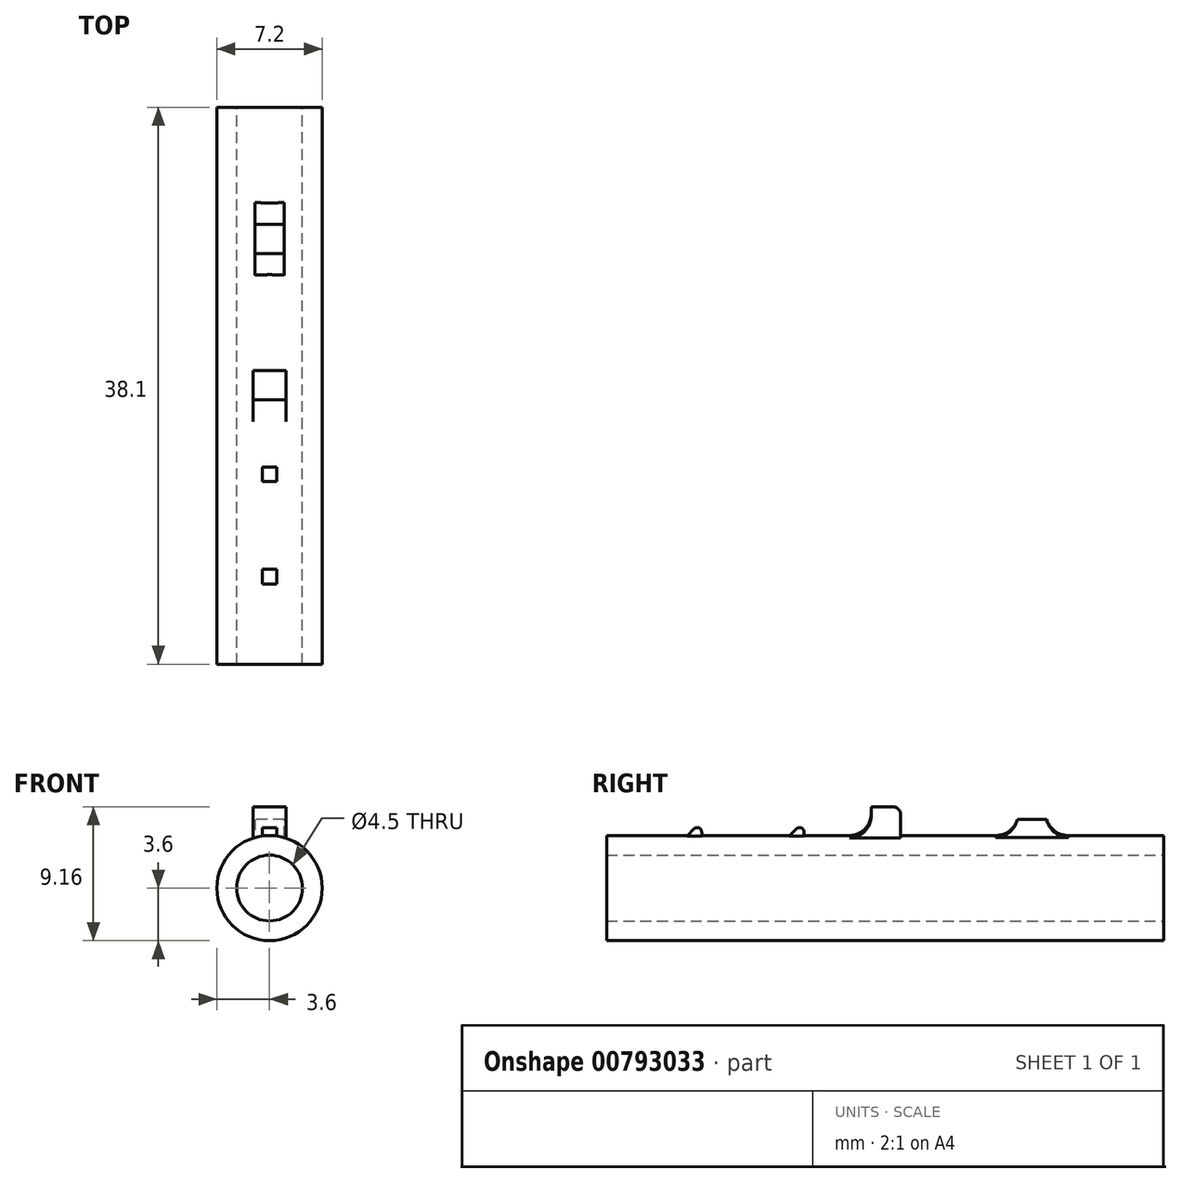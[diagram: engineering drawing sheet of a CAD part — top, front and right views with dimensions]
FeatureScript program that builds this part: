
annotation { "Feature Type Name" : "Feature", "Feature Type Description" : "" }
export const myFeature = defineFeature(function(context is Context, id is Id, definition is map)
    precondition{}
    {
        {
            var Q0;
            Q0=qCreatedBy(makeId("Front.planeOp"),FACE);
            var sketch = newSketch(context, id + "F0", { "sketchPlane" : qUnion([Q0])});
            skCircle(sketch, "E0", {"center": v(0, 0) * mm, "radius": 2.25 * mm});
            skCircle(sketch, "E1", {"center": v(0, 0) * mm, "radius": 3.6 * mm});
            skSolve(sketch);
        }
        {
            var Q0;
            Q0=makeQuery(id+"F0.imprint","IMPRINT",FACE,{"disambiguationData":[TD([[makeQuery(id+"F0.imprint","IMPRINT",EDGE,{"derivedFrom":sQuery(id+"F0.wireOp",EDGE,"E0")}),-1.0]])]});
            extrude(context, id + "F1", {"entities" : qUnion([Q0]), "depth" : 37.6 * mm, "offsetDistance" : 25.4 * mm});
        }
        {
            var Q0;
            Q0=makeQuery(id+"F1.opExtrude","CAP_FACE",FACE,{"disambiguationData":[OSD([sQuery(id+"F0.wireOp",EDGE,"E0"),sQuery(id+"F0.wireOp",EDGE,"E1")])],"isStart":false});
            var sketch = newSketch(context, id + "F2", { "sketchPlane" : qUnion([Q0])});
            skLineSegment(sketch, "E2.bottom", {"start": v(1, 4.71) * mm, "end": v(-1, 4.71) * mm});
            skLineSegment(sketch, "E2.left", {"start": v(1, 4.71) * mm, "end": v(1, 3.46) * mm});
            skLineSegment(sketch, "E2.right", {"start": v(-1, 4.71) * mm, "end": v(-1, 3.46) * mm});
            skPoint(sketch, "E2.middle", {"position": v(0, 3.6) * mm});
            skPoint(sketch, "E3", {"position": v(-1, 3.46) * mm});
            skPoint(sketch, "E4", {"position": v(1, 3.46) * mm});
            skPoint(sketch, "E2.top.end.orphan", {"position": v(-1, 2.49) * mm});
            skPoint(sketch, "E5.orphan", {"position": v(1, 2.49) * mm});
            skSolve(sketch);
        }
        {
            var Q0;
            Q0=makeQuery(id+"F2.imprint","IMPRINT",FACE,{"disambiguationData":[TD([[makeQuery(id+"F2.imprint","IMPRINT",EDGE,{"derivedFrom":sQuery(id+"F2.wireOp",EDGE,"E2.bottom")}),1.0]])]});
            extrude(context, id + "F3", {"entities" : qUnion([Q0]), "operationType" : NewBodyOperationType.ADD, "oppositeDirection" : true, "depth" : 37.05 * mm, "offsetDistance" : 25 * mm});
        }
        {
            var Q0;
            {var subQ0=sQuery(id+"F0.wireOp",EDGE,"E1");Q0=makeQuery(id+"F3.boolean.opBoolean","MERGE",FACE,{"derivedFrom":[makeQuery(id+"F1.opExtrude","CAP_FACE",FACE,{"disambiguationData":[OSD([sQuery(id+"F0.wireOp",EDGE,"E0"),subQ0])],"isStart":false}),makeQuery(id+"F3.opExtrude","CAP_FACE",FACE,{"disambiguationData":[OSD([subQ0,sQuery(id+"F2.wireOp",EDGE,"E2.bottom"),sQuery(id+"F2.wireOp",EDGE,"E2.left"),sQuery(id+"F2.wireOp",EDGE,"E2.right")])],"isStart":true})]});}
            var sketch = newSketch(context, id + "F4", { "sketchPlane" : qUnion([Q0])});
            skCircle(sketch, "E6", {"center": v(0, 0) * mm, "radius": 3.6 * mm});
            skSolve(sketch);
        }
        {
            var Q0;
            Q0=makeQuery(id+"F4.imprint","IMPRINT",FACE,{"disambiguationData":[TD([[makeQuery(id+"F4.imprint","IMPRINT",EDGE,{"derivedFrom":makeQuery(id+"F3.opExtrude","CAP_EDGE",EDGE,{"disambiguationData":[OSD([sQuery(id+"F2.wireOp",EDGE,"E2.bottom")])],"isStart":true})}),1.0]])]});
            extrude(context, id + "F5", {"entities" : qUnion([Q0]), "operationType" : NewBodyOperationType.REMOVE, "oppositeDirection" : true, "depth" : 27.6 * mm, "offsetDistance" : 25 * mm});
        }
        {
            var Q0;
            Q0=makeQuery(id+"F3.opExtrude","CAP_FACE",FACE,{"disambiguationData":[OSD([sQuery(id+"F0.wireOp",EDGE,"E1"),sQuery(id+"F2.wireOp",EDGE,"E2.bottom"),sQuery(id+"F2.wireOp",EDGE,"E2.left"),sQuery(id+"F2.wireOp",EDGE,"E2.right")])],"isStart":false});
            extrude(context, id + "F6", {"entities" : qUnion([Q0]), "operationType" : NewBodyOperationType.REMOVE, "oppositeDirection" : true, "depth" : 7.45 * mm, "offsetDistance" : 25 * mm});
        }
        {
            var Q0;
            {var subQ0=sQuery(id+"F0.wireOp",EDGE,"E1");Q0=makeQuery(id+"F3.boolean.opBoolean","MERGE",FACE,{"derivedFrom":[makeQuery(id+"F1.opExtrude","CAP_FACE",FACE,{"disambiguationData":[OSD([sQuery(id+"F0.wireOp",EDGE,"E0"),subQ0])],"isStart":false}),makeQuery(id+"F3.opExtrude","CAP_FACE",FACE,{"disambiguationData":[OSD([subQ0,sQuery(id+"F2.wireOp",EDGE,"E2.bottom"),sQuery(id+"F2.wireOp",EDGE,"E2.left"),sQuery(id+"F2.wireOp",EDGE,"E2.right")])],"isStart":true})]});}
            var sketch = newSketch(context, id + "F7", { "sketchPlane" : qUnion([Q0])});
            skLineSegment(sketch, "E7.bottom", {"start": v(1.12, 5.56) * mm, "end": v(-1.12, 5.56) * mm});
            skLineSegment(sketch, "E7.left", {"start": v(1.12, 5.56) * mm, "end": v(1.12, 3.42) * mm});
            skLineSegment(sketch, "E7.right", {"start": v(-1.12, 5.56) * mm, "end": v(-1.12, 3.42) * mm});
            skPoint(sketch, "E7.middle", {"position": v(0, 3.6) * mm});
            skPoint(sketch, "E8", {"position": v(-1.12, 3.42) * mm});
            skPoint(sketch, "E9", {"position": v(1.12, 3.42) * mm});
            skPoint(sketch, "E7.top.end.orphan", {"position": v(-1.12, 1.64) * mm});
            skPoint(sketch, "E10.orphan", {"position": v(1.12, 1.64) * mm});
            skCircle(sketch, "E11", {"center": v(0, 0) * mm, "radius": 3.6 * mm});
            skSolve(sketch);
        }
        {
            var Q0;
            Q0=makeQuery(id+"F7.imprint","IMPRINT",FACE,{"disambiguationData":[TD([[makeQuery(id+"F7.imprint","IMPRINT",EDGE,{"derivedFrom":sQuery(id+"F7.wireOp",EDGE,"E7.bottom")}),1.0]])]});
            extrude(context, id + "F8", {"entities" : qUnion([Q0]), "operationType" : NewBodyOperationType.ADD, "oppositeDirection" : true, "depth" : 19.6 * mm, "offsetDistance" : 25 * mm});
        }
        {
            var Q0;
            {var subQ0=sQuery(id+"F0.wireOp",EDGE,"E1");Q0=makeQuery(id+"F8.boolean.opBoolean","MERGE",FACE,{"derivedFrom":[makeQuery(id+"F3.boolean.opBoolean","MERGE",FACE,{"derivedFrom":[makeQuery(id+"F1.opExtrude","CAP_FACE",FACE,{"disambiguationData":[OSD([sQuery(id+"F0.wireOp",EDGE,"E0"),subQ0])],"isStart":false}),makeQuery(id+"F3.opExtrude","CAP_FACE",FACE,{"disambiguationData":[OSD([subQ0,sQuery(id+"F2.wireOp",EDGE,"E2.bottom"),sQuery(id+"F2.wireOp",EDGE,"E2.left"),sQuery(id+"F2.wireOp",EDGE,"E2.right")])],"isStart":true})]}),makeQuery(id+"F8.opExtrude","CAP_FACE",FACE,{"disambiguationData":[OSD([sQuery(id+"F7.wireOp",EDGE,"E7.bottom"),sQuery(id+"F7.wireOp",EDGE,"E7.left"),sQuery(id+"F7.wireOp",EDGE,"E7.right"),sQuery(id+"F7.wireOp",EDGE,"E11")])],"isStart":true})]});}
            var sketch = newSketch(context, id + "F9", { "sketchPlane" : qUnion([Q0])});
            skCircle(sketch, "E12", {"center": v(0, 0) * mm, "radius": 3.6 * mm});
            skSolve(sketch);
        }
        {
            var Q0;
            Q0=makeQuery(id+"F9.imprint","IMPRINT",FACE,{"disambiguationData":[TD([[makeQuery(id+"F9.imprint","IMPRINT",EDGE,{"derivedFrom":makeQuery(id+"F8.opExtrude","CAP_EDGE",EDGE,{"disambiguationData":[OSD([sQuery(id+"F7.wireOp",EDGE,"E7.bottom")])],"isStart":true})}),1.0]])]});
            extrude(context, id + "F10", {"entities" : qUnion([Q0]), "operationType" : NewBodyOperationType.REMOVE, "oppositeDirection" : true, "depth" : 17.6 * mm, "offsetDistance" : 25 * mm});
        }
        {
            var Q0;
            {var subQ0=sQuery(id+"F0.wireOp",EDGE,"E1");Q0=makeQuery(id+"F8.boolean.opBoolean","MERGE",FACE,{"derivedFrom":[makeQuery(id+"F3.boolean.opBoolean","MERGE",FACE,{"derivedFrom":[makeQuery(id+"F1.opExtrude","CAP_FACE",FACE,{"disambiguationData":[OSD([sQuery(id+"F0.wireOp",EDGE,"E0"),subQ0])],"isStart":false}),makeQuery(id+"F3.opExtrude","CAP_FACE",FACE,{"disambiguationData":[OSD([subQ0,sQuery(id+"F2.wireOp",EDGE,"E2.bottom"),sQuery(id+"F2.wireOp",EDGE,"E2.left"),sQuery(id+"F2.wireOp",EDGE,"E2.right")])],"isStart":true})]}),makeQuery(id+"F8.opExtrude","CAP_FACE",FACE,{"disambiguationData":[OSD([sQuery(id+"F7.wireOp",EDGE,"E7.bottom"),sQuery(id+"F7.wireOp",EDGE,"E7.left"),sQuery(id+"F7.wireOp",EDGE,"E7.right"),sQuery(id+"F7.wireOp",EDGE,"E11")])],"isStart":true})]});}
            var sketch = newSketch(context, id + "F11", { "sketchPlane" : qUnion([Q0])});
            skLineSegment(sketch, "E13.bottom", {"start": v(0.5, 4.57) * mm, "end": v(-0.5, 4.57) * mm});
            skLineSegment(sketch, "E13.left", {"start": v(0.5, 4.57) * mm, "end": v(0.5, 3.57) * mm});
            skLineSegment(sketch, "E13.right", {"start": v(-0.5, 4.57) * mm, "end": v(-0.5, 3.57) * mm});
            skPoint(sketch, "E13.middle", {"position": v(0, 3.6) * mm});
            skPoint(sketch, "E14", {"position": v(-0.5, 3.57) * mm});
            skPoint(sketch, "E15", {"position": v(0.5, 3.57) * mm});
            skPoint(sketch, "E13.top.end.orphan", {"position": v(-0.5, 2.63) * mm});
            skPoint(sketch, "E16.orphan", {"position": v(0.5, 2.63) * mm});
            skCircle(sketch, "E17", {"center": v(0, 0) * mm, "radius": 3.6 * mm});
            skSolve(sketch);
        }
        {
            var Q0;
            Q0=makeQuery(id+"F11.imprint","IMPRINT",FACE,{"disambiguationData":[TD([[makeQuery(id+"F11.imprint","IMPRINT",EDGE,{"derivedFrom":sQuery(id+"F11.wireOp",EDGE,"E13.bottom")}),1.0]])]});
            extrude(context, id + "F12", {"entities" : qUnion([Q0]), "operationType" : NewBodyOperationType.ADD, "oppositeDirection" : true, "depth" : 13 * mm, "offsetDistance" : 25 * mm});
        }
        {
            var Q0;
            {var subQ0=sQuery(id+"F0.wireOp",EDGE,"E1");Q0=makeQuery(id+"F12.boolean.opBoolean","MERGE",FACE,{"derivedFrom":[makeQuery(id+"F8.boolean.opBoolean","MERGE",FACE,{"derivedFrom":[makeQuery(id+"F3.boolean.opBoolean","MERGE",FACE,{"derivedFrom":[makeQuery(id+"F1.opExtrude","CAP_FACE",FACE,{"disambiguationData":[OSD([sQuery(id+"F0.wireOp",EDGE,"E0"),subQ0])],"isStart":false}),makeQuery(id+"F3.opExtrude","CAP_FACE",FACE,{"disambiguationData":[OSD([subQ0,sQuery(id+"F2.wireOp",EDGE,"E2.bottom"),sQuery(id+"F2.wireOp",EDGE,"E2.left"),sQuery(id+"F2.wireOp",EDGE,"E2.right")])],"isStart":true})]}),makeQuery(id+"F8.opExtrude","CAP_FACE",FACE,{"disambiguationData":[OSD([sQuery(id+"F7.wireOp",EDGE,"E7.bottom"),sQuery(id+"F7.wireOp",EDGE,"E7.left"),sQuery(id+"F7.wireOp",EDGE,"E7.right"),sQuery(id+"F7.wireOp",EDGE,"E11")])],"isStart":true})]}),makeQuery(id+"F12.opExtrude","CAP_FACE",FACE,{"disambiguationData":[OSD([sQuery(id+"F11.wireOp",EDGE,"E13.bottom"),sQuery(id+"F11.wireOp",EDGE,"E13.left"),sQuery(id+"F11.wireOp",EDGE,"E13.right"),sQuery(id+"F11.wireOp",EDGE,"E17")])],"isStart":true})]});}
            var sketch = newSketch(context, id + "F13", { "sketchPlane" : qUnion([Q0])});
            skCircle(sketch, "E18", {"center": v(0, 0) * mm, "radius": 3.6 * mm});
            skSolve(sketch);
        }
        {
            var Q0;
            Q0=makeQuery(id+"F13.imprint","IMPRINT",FACE,{"disambiguationData":[TD([[makeQuery(id+"F13.imprint","IMPRINT",EDGE,{"derivedFrom":makeQuery(id+"F12.opExtrude","CAP_EDGE",EDGE,{"disambiguationData":[OSD([sQuery(id+"F11.wireOp",EDGE,"E13.bottom")])],"isStart":true})}),1.0]])]});
            extrude(context, id + "F14", {"entities" : qUnion([Q0]), "operationType" : NewBodyOperationType.REMOVE, "oppositeDirection" : true, "depth" : 12 * mm, "offsetDistance" : 25 * mm});
        }
        {
            var Q0;
            {var subQ0=sQuery(id+"F0.wireOp",EDGE,"E1");Q0=makeQuery(id+"F12.boolean.opBoolean","MERGE",FACE,{"derivedFrom":[makeQuery(id+"F8.boolean.opBoolean","MERGE",FACE,{"derivedFrom":[makeQuery(id+"F3.boolean.opBoolean","MERGE",FACE,{"derivedFrom":[makeQuery(id+"F1.opExtrude","CAP_FACE",FACE,{"disambiguationData":[OSD([sQuery(id+"F0.wireOp",EDGE,"E0"),subQ0])],"isStart":false}),makeQuery(id+"F3.opExtrude","CAP_FACE",FACE,{"disambiguationData":[OSD([subQ0,sQuery(id+"F2.wireOp",EDGE,"E2.bottom"),sQuery(id+"F2.wireOp",EDGE,"E2.left"),sQuery(id+"F2.wireOp",EDGE,"E2.right")])],"isStart":true})]}),makeQuery(id+"F8.opExtrude","CAP_FACE",FACE,{"disambiguationData":[OSD([sQuery(id+"F7.wireOp",EDGE,"E7.bottom"),sQuery(id+"F7.wireOp",EDGE,"E7.left"),sQuery(id+"F7.wireOp",EDGE,"E7.right"),sQuery(id+"F7.wireOp",EDGE,"E11")])],"isStart":true})]}),makeQuery(id+"F12.opExtrude","CAP_FACE",FACE,{"disambiguationData":[OSD([sQuery(id+"F11.wireOp",EDGE,"E13.bottom"),sQuery(id+"F11.wireOp",EDGE,"E13.left"),sQuery(id+"F11.wireOp",EDGE,"E13.right"),sQuery(id+"F11.wireOp",EDGE,"E17")])],"isStart":true})]});}
            var sketch = newSketch(context, id + "F15", { "sketchPlane" : qUnion([Q0])});
            skLineSegment(sketch, "E19.bottom", {"start": v(0.5, 4.57) * mm, "end": v(-0.5, 4.57) * mm});
            skLineSegment(sketch, "E19.left", {"start": v(0.5, 4.57) * mm, "end": v(0.5, 3.57) * mm});
            skLineSegment(sketch, "E19.right", {"start": v(-0.5, 4.57) * mm, "end": v(-0.5, 3.57) * mm});
            skPoint(sketch, "E19.middle", {"position": v(0, 3.6) * mm});
            skPoint(sketch, "E20", {"position": v(-0.5, 3.57) * mm});
            skPoint(sketch, "E21", {"position": v(0.5, 3.57) * mm});
            skPoint(sketch, "E19.top.end.orphan", {"position": v(-0.5, 2.63) * mm});
            skPoint(sketch, "E22.orphan", {"position": v(0.5, 2.63) * mm});
            skSolve(sketch);
        }
        {
            var Q0;
            Q0=makeQuery(id+"F15.imprint","IMPRINT",FACE,{"disambiguationData":[TD([[makeQuery(id+"F15.imprint","IMPRINT",EDGE,{"derivedFrom":sQuery(id+"F15.wireOp",EDGE,"E19.bottom")}),1.0]])]});
            extrude(context, id + "F16", {"entities" : qUnion([Q0]), "operationType" : NewBodyOperationType.ADD, "oppositeDirection" : true, "depth" : 6 * mm, "offsetDistance" : 25 * mm});
        }
        {
            var Q0;
            {var subQ0=sQuery(id+"F0.wireOp",EDGE,"E1");Q0=makeQuery(id+"F16.boolean.opBoolean","MERGE",FACE,{"derivedFrom":[makeQuery(id+"F12.boolean.opBoolean","MERGE",FACE,{"derivedFrom":[makeQuery(id+"F8.boolean.opBoolean","MERGE",FACE,{"derivedFrom":[makeQuery(id+"F3.boolean.opBoolean","MERGE",FACE,{"derivedFrom":[makeQuery(id+"F1.opExtrude","CAP_FACE",FACE,{"disambiguationData":[OSD([sQuery(id+"F0.wireOp",EDGE,"E0"),subQ0])],"isStart":false}),makeQuery(id+"F3.opExtrude","CAP_FACE",FACE,{"disambiguationData":[OSD([subQ0,sQuery(id+"F2.wireOp",EDGE,"E2.bottom"),sQuery(id+"F2.wireOp",EDGE,"E2.left"),sQuery(id+"F2.wireOp",EDGE,"E2.right")])],"isStart":true})]}),makeQuery(id+"F8.opExtrude","CAP_FACE",FACE,{"disambiguationData":[OSD([sQuery(id+"F7.wireOp",EDGE,"E7.bottom"),sQuery(id+"F7.wireOp",EDGE,"E7.left"),sQuery(id+"F7.wireOp",EDGE,"E7.right"),sQuery(id+"F7.wireOp",EDGE,"E11")])],"isStart":true})]}),makeQuery(id+"F12.opExtrude","CAP_FACE",FACE,{"disambiguationData":[OSD([sQuery(id+"F11.wireOp",EDGE,"E13.bottom"),sQuery(id+"F11.wireOp",EDGE,"E13.left"),sQuery(id+"F11.wireOp",EDGE,"E13.right"),sQuery(id+"F11.wireOp",EDGE,"E17")])],"isStart":true})]}),makeQuery(id+"F16.opExtrude","CAP_FACE",FACE,{"disambiguationData":[OSD([subQ0,sQuery(id+"F4.wireOp",EDGE,"E6"),sQuery(id+"F9.wireOp",EDGE,"E12"),sQuery(id+"F13.wireOp",EDGE,"E18"),sQuery(id+"F15.wireOp",EDGE,"E19.bottom"),sQuery(id+"F15.wireOp",EDGE,"E19.left"),sQuery(id+"F15.wireOp",EDGE,"E19.right")])],"isStart":true})]});}
            var sketch = newSketch(context, id + "F17", { "sketchPlane" : qUnion([Q0])});
            skCircle(sketch, "E23", {"center": v(0, 0) * mm, "radius": 3.6 * mm});
            skSolve(sketch);
        }
        {
            var Q0;
            Q0=makeQuery(id+"F17.imprint","IMPRINT",FACE,{"disambiguationData":[TD([[makeQuery(id+"F17.imprint","IMPRINT",EDGE,{"derivedFrom":makeQuery(id+"F16.opExtrude","CAP_EDGE",EDGE,{"disambiguationData":[OSD([sQuery(id+"F15.wireOp",EDGE,"E19.bottom")])],"isStart":true})}),1.0]])]});
            extrude(context, id + "F18", {"entities" : qUnion([Q0]), "operationType" : NewBodyOperationType.REMOVE, "oppositeDirection" : true, "depth" : 5 * mm, "offsetDistance" : 25 * mm});
        }
        {
            var Q0;
            Q0=makeQuery(id+"F16.opExtrude","SWEPT_FACE",FACE,{"disambiguationData":[OSD([sQuery(id+"F15.wireOp",EDGE,"E19.left")])]});
            var sketch = newSketch(context, id + "F19", { "sketchPlane" : qUnion([Q0])});
            skLineSegment(sketch, "E24", {"start": v(-31.6, 4.57) * mm, "end": v(-32.6, 3.57) * mm});
            skSolve(sketch);
        }
        {
            var Q0;
            Q0=makeQuery(id+"F19.imprint","IMPRINT",FACE,{"disambiguationData":[TD([[makeQuery(id+"F19.imprint","IMPRINT",EDGE,{"derivedFrom":sQuery(id+"F19.wireOp",EDGE,"E24")}),-1.0]])]});
            extrude(context, id + "F20", {"entities" : qUnion([Q0]), "operationType" : NewBodyOperationType.REMOVE, "oppositeDirection" : true, "depth" : 25 * mm, "offsetDistance" : 25 * mm});
        }
        {
            var Q0;
            Q0=makeQuery(id+"F12.opExtrude","SWEPT_FACE",FACE,{"disambiguationData":[OSD([sQuery(id+"F11.wireOp",EDGE,"E13.left")])]});
            var sketch = newSketch(context, id + "F21", { "sketchPlane" : qUnion([Q0])});
            skLineSegment(sketch, "E25", {"start": v(-24.6, 4.57) * mm, "end": v(-25.6, 3.57) * mm});
            skSolve(sketch);
        }
        {
            var Q0;
            Q0=makeQuery(id+"F21.imprint","IMPRINT",FACE,{"disambiguationData":[TD([[makeQuery(id+"F21.imprint","IMPRINT",EDGE,{"derivedFrom":sQuery(id+"F21.wireOp",EDGE,"E25")}),-1.0]])]});
            extrude(context, id + "F22", {"entities" : qUnion([Q0]), "operationType" : NewBodyOperationType.REMOVE, "oppositeDirection" : true, "depth" : 25 * mm, "offsetDistance" : 25 * mm});
        }
        {
            var Q0;
            {var subQ0=sQuery(id+"F15.wireOp",EDGE,"E19.bottom");Q0=makeQuery(id+"F20.boolean.opBoolean","MERGE",EDGE,{"derivedFrom":[makeQuery(id+"F16.opExtrude","CAP_EDGE",EDGE,{"disambiguationData":[OSD([subQ0])],"isStart":false}),makeQuery(id+"F20.opExtrude","SWEPT_EDGE",EDGE,{"disambiguationData":[OSD([subQ0,sQuery(id+"F15.wireOp",EDGE,"E19.left"),sQuery(id+"F19.wireOp",EDGE,"E24")])]})]});}
            var Q1;
            {var subQ0=sQuery(id+"F11.wireOp",EDGE,"E13.bottom");Q1=makeQuery(id+"F22.boolean.opBoolean","MERGE",EDGE,{"derivedFrom":[makeQuery(id+"F12.opExtrude","CAP_EDGE",EDGE,{"disambiguationData":[OSD([subQ0])],"isStart":false}),makeQuery(id+"F22.opExtrude","SWEPT_EDGE",EDGE,{"disambiguationData":[OSD([subQ0,sQuery(id+"F11.wireOp",EDGE,"E13.left"),sQuery(id+"F21.wireOp",EDGE,"E25")])]})]});}
            fillet(context, id + "F23", {"entities" : qUnion([Q0, Q1]), "radius" : 0.3 * mm, "tangentPropagation" : true, "allowEdgeOverflow" : false});
        }
        {
            var Q0;
            Q0=makeQuery(id+"F8.opExtrude","CAP_EDGE",EDGE,{"disambiguationData":[OSD([sQuery(id+"F7.wireOp",EDGE,"E7.bottom")])],"isStart":false});
            var Q1;
            Q1=makeQuery(id+"F10.boolean.opBoolean","COPY",EDGE,{"derivedFrom":makeQuery(id+"F10.opExtrude","CAP_EDGE",EDGE,{"disambiguationData":[OSD([sQuery(id+"F7.wireOp",EDGE,"E7.bottom")])],"isStart":false})});
            fillet(context, id + "F24", {"entities" : qUnion([Q0, Q1]), "radius" : 0.5 * mm, "tangentPropagation" : true, "allowEdgeOverflow" : false});
        }
        {
            var Q0;
            Q0=makeQuery(id+"F8.opExtrude","CAP_EDGE",EDGE,{"disambiguationData":[OSD([sQuery(id+"F7.wireOp",EDGE,"E11")])],"isStart":false});
            var Q1;
            Q1=makeQuery(id+"F10.boolean.opBoolean","COPY",EDGE,{"derivedFrom":makeQuery(id+"F10.opExtrude","CAP_EDGE",EDGE,{"disambiguationData":[OSD([sQuery(id+"F9.wireOp",EDGE,"E12")])],"isStart":false})});
            var Q2;
            Q2=makeQuery(id+"F5.boolean.opBoolean","COPY",EDGE,{"derivedFrom":makeQuery(id+"F5.opExtrude","CAP_EDGE",EDGE,{"disambiguationData":[OSD([sQuery(id+"F4.wireOp",EDGE,"E6")])],"isStart":false})});
            var Q3;
            Q3=makeQuery(id+"F6.boolean.opBoolean","COPY",EDGE,{"derivedFrom":makeQuery(id+"F6.opExtrude","CAP_EDGE",EDGE,{"disambiguationData":[OSD([sQuery(id+"F0.wireOp",EDGE,"E1")])],"isStart":false})});
            fillet(context, id + "F25", {"entities" : qUnion([Q0, Q1, Q2, Q3]), "radius" : 1.5 * mm, "tangentPropagation" : true, "allowEdgeOverflow" : false});
        }
        {
            var Q0;
            {var subQ0=sQuery(id+"F15.wireOp",EDGE,"E19.right");var subQ1=sQuery(id+"F15.wireOp",EDGE,"E19.left");var subQ2=sQuery(id+"F15.wireOp",EDGE,"E19.bottom");var subQ3=sQuery(id+"F13.wireOp",EDGE,"E18");var subQ4=sQuery(id+"F9.wireOp",EDGE,"E12");var subQ5=sQuery(id+"F4.wireOp",EDGE,"E6");var subQ6=sQuery(id+"F0.wireOp",EDGE,"E1");var subQ7=sQuery(id+"F11.wireOp",EDGE,"E17");var subQ8=sQuery(id+"F11.wireOp",EDGE,"E13.right");var subQ9=sQuery(id+"F11.wireOp",EDGE,"E13.left");var subQ10=sQuery(id+"F11.wireOp",EDGE,"E13.bottom");var subQ11=sQuery(id+"F7.wireOp",EDGE,"E11");var subQ12=sQuery(id+"F7.wireOp",EDGE,"E7.right");var subQ13=sQuery(id+"F7.wireOp",EDGE,"E7.left");var subQ14=sQuery(id+"F7.wireOp",EDGE,"E7.bottom");var subQ15=sQuery(id+"F2.wireOp",EDGE,"E2.right");var subQ16=sQuery(id+"F2.wireOp",EDGE,"E2.left");var subQ17=sQuery(id+"F2.wireOp",EDGE,"E2.bottom");Q0=makeQuery(id+"FrB15HOE70lnXQ4_1.1.F16.boolean.opBoolean","MERGE",FACE,{"derivedFrom":[makeQuery(id+"FrB15HOE70lnXQ4_1.1.F12.boolean.opBoolean","MERGE",FACE,{"derivedFrom":[makeQuery(id+"FrB15HOE70lnXQ4_1.1.F8.boolean.opBoolean","MERGE",FACE,{"derivedFrom":[makeQuery(id+"FrB15HOE70lnXQ4_1.1.F3.boolean.opBoolean","MERGE",FACE,{"derivedFrom":[makeQuery(id+"F16.boolean.opBoolean","MERGE",FACE,{"derivedFrom":[makeQuery(id+"F12.boolean.opBoolean","MERGE",FACE,{"derivedFrom":[makeQuery(id+"F8.boolean.opBoolean","MERGE",FACE,{"derivedFrom":[makeQuery(id+"F3.boolean.opBoolean","MERGE",FACE,{"derivedFrom":[makeQuery(id+"F1.opExtrude","CAP_FACE",FACE,{"disambiguationData":[OSD([sQuery(id+"F0.wireOp",EDGE,"E0"),subQ6])],"isStart":false}),makeQuery(id+"F3.opExtrude","CAP_FACE",FACE,{"disambiguationData":[OSD([subQ6,subQ17,subQ16,subQ15])],"isStart":true})]}),makeQuery(id+"F8.opExtrude","CAP_FACE",FACE,{"disambiguationData":[OSD([subQ14,subQ13,subQ12,subQ11])],"isStart":true})]}),makeQuery(id+"F12.opExtrude","CAP_FACE",FACE,{"disambiguationData":[OSD([subQ10,subQ9,subQ8,subQ7])],"isStart":true})]}),makeQuery(id+"F16.opExtrude","CAP_FACE",FACE,{"disambiguationData":[OSD([subQ6,subQ5,subQ4,subQ3,subQ2,subQ1,subQ0])],"isStart":true})]}),makeQuery(id+"FrB15HOE70lnXQ4_1.1.F3.opExtrude","CAP_FACE",FACE,{"disambiguationData":[OSD([subQ6,subQ17,subQ16,subQ15])],"isStart":true})]}),makeQuery(id+"FrB15HOE70lnXQ4_1.1.F8.opExtrude","CAP_FACE",FACE,{"disambiguationData":[OSD([subQ14,subQ13,subQ12,subQ11])],"isStart":true})]}),makeQuery(id+"FrB15HOE70lnXQ4_1.1.F12.opExtrude","CAP_FACE",FACE,{"disambiguationData":[OSD([subQ10,subQ9,subQ8,subQ7])],"isStart":true})]}),makeQuery(id+"FrB15HOE70lnXQ4_1.1.F16.opExtrude","CAP_FACE",FACE,{"disambiguationData":[OSD([subQ6,subQ5,subQ4,subQ3,subQ2,subQ1,subQ0])],"isStart":true})]});}
            extrude(context, id + "F26", {"entities" : qUnion([Q0]), "operationType" : NewBodyOperationType.ADD, "depth" : 0.5 * mm, "offsetDistance" : 25 * mm});
        }
    });
